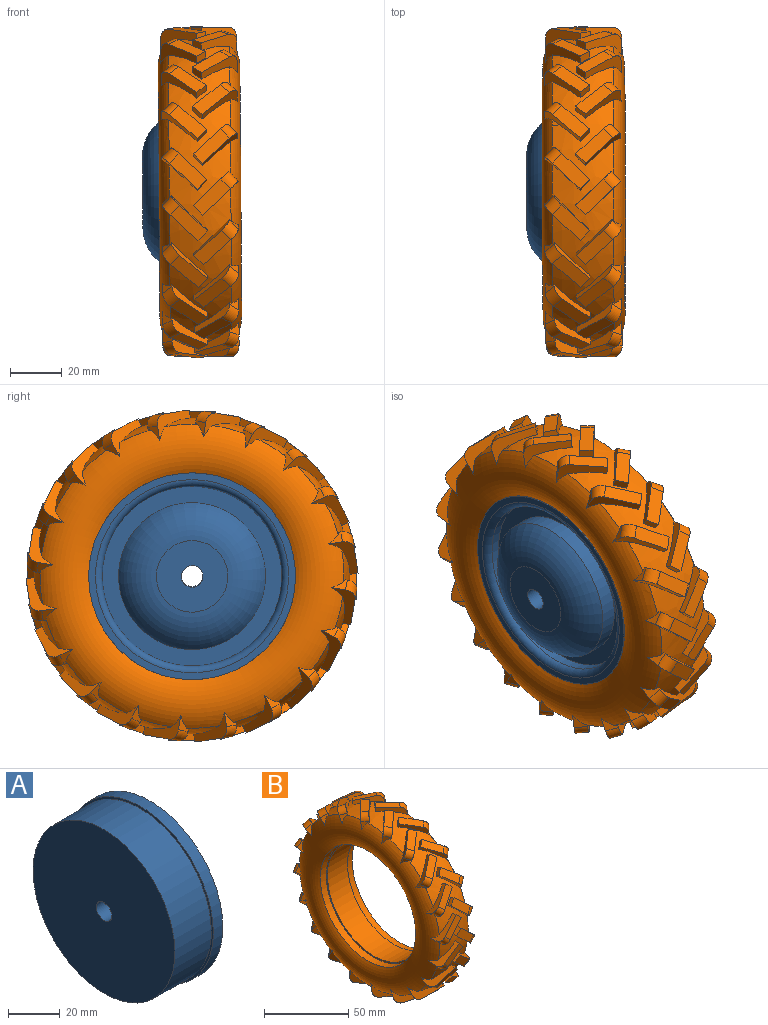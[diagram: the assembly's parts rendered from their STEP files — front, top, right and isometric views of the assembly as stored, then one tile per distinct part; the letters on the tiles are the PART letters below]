
ASSEMBLY  parts=2 mates=2
PART A: 12 faces, bbox 33.7x80.8x80.8 mm
  f0: cylinder r=39.98mm len=79.95mm, axis (1,0,0), area 1321.2mm2, adj f1,f2
  f1: plane 79.95x79.95mm, normal (-1,0,0), area 260.8mm2, adj f0,f3
  f2: plane 79.95x79.95mm, normal (1,0,0), area 638.9mm2, adj f0,f11
  f3: cylinder r=38.92mm len=77.85mm, axis (1,0,0), area 4888.4mm2, adj f1,f4
  f4: plane 77.85x77.85mm, normal (-1,0,0), area 4704.1mm2, adj f3,f7
  f5: plane 27.65x27.65mm, normal (1,0,0), area 545mm2, adj f6,f7
  f6: torus R=13.83mm, axis (-1,0,0), area 2421.4mm2, adj f5,f9
  f7: cylinder r=4.21mm len=33.66mm, axis (-1,0,0), area 890.1mm2, adj f4,f5
  f8: cylinder r=34.72mm len=69.43mm, axis (1,0,0), area 803.1mm2, adj f10,f11
  f9: cylinder r=28.4mm len=56.81mm, axis (1,0,0), area 1126.5mm2, adj f6,f10
  f10: plane 69.43x69.43mm, normal (1,0,0), area 1251.7mm2, adj f8,f9
  f11: torus R=37.35mm, axis (1,0,0), area 925.9mm2, adj f2,f8
PART B: 250 faces, bbox 31.7x129.1x129.1 mm
  f0: torus R=48.39mm, axis (-1,0,0), area 6003.5mm2, adj f2,f4,f7,f8,f19,f20,f31,f32
  f1: cylinder r=38.92mm len=77.85mm, axis (1,0,0), area 4116.5mm2, adj f247,f249
  f2: torus R=28.4mm, axis (-1,0,0), area 5449.9mm2, adj f0,f3,f4,f5,f6,f7,f8,f9
  f3: torus R=28.4mm, axis (-1,0,0), area 4.2mm2, adj f2,f5,f195
  f4: torus R=28.4mm, axis (-1,0,0), area 0.3mm2, adj f0,f2,f175
  f5: torus R=48.39mm, axis (-1,0,0), area 6003.6mm2, adj f2,f3,f14,f15,f26,f27,f38,f39
  f6: plane 13.76x12.72mm, normal (0.69,0.11,-0.72), area 58.8mm2, adj f2,f7,f9,f10,f11
  f7: plane 5.51x4.65mm, normal (-0.73,0.11,-0.68), area 13.8mm2, adj f0,f2,f6,f8,f11
  f8: plane 13.86x12.87mm, normal (-0.69,-0.11,0.72), area 77.6mm2, adj f0,f2,f7,f9,f10,f11
  f9: plane 4.29x3.63mm, normal (0.73,-0.11,0.68), area 15.9mm2, adj f2,f6,f8,f10
  f10: plane 14.32x13.77mm, normal (0,-0.99,-0.16), area 77.5mm2, adj f6,f8,f9,f11
  f11: cylinder r=4.21mm len=6.67mm, axis (0.69,0.11,-0.72), area 34.8mm2, adj f6,f7,f8,f10
  f12: plane 3.83x3.63mm, normal (-0.73,0,0.69), area 15.9mm2, adj f2,f13,f15,f16
  f13: plane 13.76x13.01mm, normal (-0.69,0,-0.73), area 58.8mm2, adj f2,f12,f14,f16,f17
  f14: plane 5.58x3.82mm, normal (0.73,0,-0.69), area 13.8mm2, adj f2,f5,f13,f15,f17
  f15: plane 13.85x13.11mm, normal (0.69,0,0.73), area 77.6mm2, adj f2,f5,f12,f14,f16,f17
  f16: plane 14.32x13.94mm, normal (0,-1,0), area 77.5mm2, adj f12,f13,f15,f17
  f17: cylinder r=4.21mm len=6.71mm, axis (-0.69,0,-0.73), area 34.8mm2, adj f13,f14,f15,f16
  f18: plane 13.76x11.63mm, normal (0.69,0.33,-0.65), area 58.8mm2, adj f2,f19,f21,f22,f23
  f19: plane 5.94x4.97mm, normal (-0.73,0.31,-0.61), area 13.8mm2, adj f0,f2,f18,f20,f23
  f20: plane 14.72x13.86mm, normal (-0.69,-0.33,0.65), area 77.6mm2, adj f0,f2,f19,f21,f22,f23
  f21: plane 4.88x4.34mm, normal (0.73,-0.31,0.61), area 15.9mm2, adj f2,f18,f20,f22
  f22: plane 14.32x12.42mm, normal (0,-0.89,-0.45), area 77.5mm2, adj f18,f20,f21,f23
  f23: cylinder r=4.21mm len=6.8mm, axis (0.69,0.33,-0.65), area 34.8mm2, adj f18,f19,f20,f22
  f24: plane 4.64x3.96mm, normal (-0.73,-0.21,0.65), area 15.9mm2, adj f2,f25,f27,f28
  f25: plane 13.76x12.26mm, normal (-0.69,0.22,-0.69), area 58.8mm2, adj f2,f24,f26,f28,f29
  f26: plane 5.36x5.3mm, normal (0.73,0.21,-0.65), area 13.8mm2, adj f2,f5,f25,f27,f29
  f27: plane 13.85x13.42mm, normal (0.69,-0.22,0.69), area 77.6mm2, adj f2,f5,f24,f26,f28,f29
  f28: plane 14.32x13.26mm, normal (0,-0.95,-0.31), area 77.5mm2, adj f24,f25,f27,f29
  f29: cylinder r=4.21mm len=6.67mm, axis (-0.69,0.22,-0.69), area 34.8mm2, adj f25,f26,f27,f28
  f30: plane 13.76x12.87mm, normal (0.69,0.51,-0.51), area 58.8mm2, adj f2,f31,f33,f34,f35
  f31: plane 6.65x3.95mm, normal (-0.73,0.49,-0.49), area 13.8mm2, adj f0,f2,f30,f32,f35
  f32: plane 16.22x13.86mm, normal (-0.69,-0.51,0.51), area 77.6mm2, adj f0,f2,f31,f33,f34,f35
  f33: plane 5x4.77mm, normal (0.73,-0.49,0.49), area 15.9mm2, adj f2,f30,f32,f34
  f34: plane 14.32x9.86mm, normal (0,-0.71,-0.71), area 77.5mm2, adj f30,f32,f33,f35
  f35: cylinder r=4.21mm len=7.72mm, axis (0.69,0.51,-0.51), area 34.8mm2, adj f30,f31,f32,f34
  f36: plane 5x4.61mm, normal (-0.73,-0.4,0.56), area 15.9mm2, adj f2,f37,f39,f40
  f37: plane 13.76x11.84mm, normal (-0.69,0.43,-0.59), area 58.8mm2, adj f2,f36,f38,f40,f41
  f38: plane 6.37x4.51mm, normal (0.73,0.4,-0.56), area 13.8mm2, adj f2,f5,f37,f39,f41
  f39: plane 15.66x13.85mm, normal (0.69,-0.43,0.59), area 77.6mm2, adj f2,f5,f36,f38,f40,f41
  f40: plane 14.32x11.28mm, normal (0,-0.81,-0.59), area 77.5mm2, adj f36,f37,f39,f41
  f41: cylinder r=4.21mm len=7.35mm, axis (-0.69,0.43,-0.59), area 34.8mm2, adj f37,f38,f39,f40
  f42: plane 13.95x13.76mm, normal (0.69,0.65,-0.33), area 58.8mm2, adj f2,f43,f45,f46,f47
  f43: plane 6.71x3.85mm, normal (-0.73,0.61,-0.31), area 13.8mm2, adj f0,f2,f42,f44,f47
  f44: plane 16.14x13.86mm, normal (-0.69,-0.65,0.33), area 77.6mm2, adj f0,f2,f43,f45,f46,f47
  f45: plane 4.74x4.62mm, normal (0.73,-0.61,0.31), area 15.9mm2, adj f2,f42,f44,f46
  f46: plane 14.32x12.42mm, normal (0,-0.45,-0.89), area 77.5mm2, adj f42,f44,f45,f47
  f47: cylinder r=4.21mm len=7.89mm, axis (0.69,0.65,-0.33), area 34.8mm2, adj f42,f43,f44,f46
  f48: plane 4.87x4.81mm, normal (-0.73,-0.56,0.4), area 15.9mm2, adj f2,f49,f51,f52
  f49: plane 13.76x13.57mm, normal (-0.69,0.59,-0.43), area 58.8mm2, adj f2,f48,f50,f52,f53
  f50: plane 6.76x3.67mm, normal (0.73,0.56,-0.4), area 13.8mm2, adj f2,f5,f49,f51,f53
  f51: plane 16.37x13.85mm, normal (0.69,-0.59,0.43), area 77.6mm2, adj f2,f5,f48,f50,f52,f53
  f52: plane 14.32x11.28mm, normal (0,-0.59,-0.81), area 77.5mm2, adj f48,f49,f51,f53
  f53: cylinder r=4.21mm len=7.9mm, axis (-0.69,0.59,-0.43), area 34.8mm2, adj f49,f50,f51,f52
  f54: plane 13.76x13.66mm, normal (0.69,0.72,-0.11), area 58.8mm2, adj f2,f55,f57,f58,f59
  f55: plane 6.11x3.93mm, normal (-0.73,0.68,-0.11), area 13.8mm2, adj f0,f2,f54,f56,f59
  f56: plane 14.48x13.86mm, normal (-0.69,-0.72,0.11), area 77.6mm2, adj f0,f2,f55,f57,f58,f59
  f57: plane 4.24x3.8mm, normal (0.73,-0.68,0.11), area 15.9mm2, adj f2,f54,f56,f58
  f58: plane 14.32x13.77mm, normal (0,-0.16,-0.99), area 77.5mm2, adj f54,f56,f57,f59
  f59: cylinder r=4.21mm len=7.29mm, axis (0.69,0.72,-0.11), area 34.8mm2, adj f54,f55,f56,f58
  f60: plane 4.55x4.26mm, normal (-0.73,-0.65,0.21), area 15.9mm2, adj f2,f61,f63,f64
  f61: plane 13.98x13.76mm, normal (-0.69,0.69,-0.22), area 58.8mm2, adj f2,f60,f62,f64,f65
  f62: plane 6.49x3.94mm, normal (0.73,0.65,-0.21), area 13.8mm2, adj f2,f5,f61,f63,f65
  f63: plane 15.49x13.85mm, normal (0.69,-0.69,0.22), area 77.6mm2, adj f2,f5,f60,f62,f64,f65
  f64: plane 14.32x13.26mm, normal (0,-0.31,-0.95), area 77.5mm2, adj f60,f61,f63,f65
  f65: cylinder r=4.21mm len=7.69mm, axis (-0.69,0.69,-0.22), area 34.8mm2, adj f61,f62,f63,f64
  f66: plane 13.76x12.72mm, normal (0.69,0.72,0.11), area 58.8mm2, adj f2,f67,f69,f70,f71
  f67: plane 5.51x4.65mm, normal (-0.73,0.68,0.11), area 13.8mm2, adj f0,f2,f66,f68,f71
  f68: plane 13.86x12.87mm, normal (-0.69,-0.72,-0.11), area 77.6mm2, adj f0,f2,f67,f69,f70,f71
  f69: plane 4.29x3.63mm, normal (0.73,-0.68,-0.11), area 15.9mm2, adj f2,f66,f68,f70
  f70: plane 14.32x13.77mm, normal (0,0.16,-0.99), area 77.5mm2, adj f66,f68,f69,f71
  f71: cylinder r=4.21mm len=6.67mm, axis (0.69,0.72,0.11), area 34.8mm2, adj f66,f67,f68,f70
  f72: plane 3.83x3.63mm, normal (-0.73,-0.69,0), area 15.9mm2, adj f2,f73,f75,f76
  f73: plane 13.76x13.01mm, normal (-0.69,0.73,0), area 58.8mm2, adj f2,f72,f74,f76,f77
  f74: plane 5.58x3.82mm, normal (0.73,0.69,0), area 13.8mm2, adj f2,f5,f73,f75,f77
  f75: plane 13.85x13.11mm, normal (0.69,-0.73,0), area 77.6mm2, adj f2,f5,f72,f74,f76,f77
  f76: plane 14.32x13.94mm, normal (0,0,-1), area 77.5mm2, adj f72,f73,f75,f77
  f77: cylinder r=4.21mm len=6.71mm, axis (-0.69,0.73,0), area 34.8mm2, adj f73,f74,f75,f76
  f78: plane 13.76x11.63mm, normal (0.69,0.65,0.33), area 58.8mm2, adj f2,f79,f81,f82,f83
  f79: plane 5.94x4.97mm, normal (-0.73,0.61,0.31), area 13.8mm2, adj f0,f2,f78,f80,f83
  f80: plane 14.72x13.86mm, normal (-0.69,-0.65,-0.33), area 77.6mm2, adj f0,f2,f79,f81,f82,f83
  f81: plane 4.88x4.34mm, normal (0.73,-0.61,-0.31), area 15.9mm2, adj f2,f78,f80,f82
  f82: plane 14.32x12.42mm, normal (0,0.45,-0.89), area 77.5mm2, adj f78,f80,f81,f83
  f83: cylinder r=4.21mm len=6.8mm, axis (0.69,0.65,0.33), area 34.8mm2, adj f78,f79,f80,f82
  f84: plane 4.64x3.96mm, normal (-0.73,-0.65,-0.21), area 15.9mm2, adj f2,f85,f87,f88
  f85: plane 13.76x12.26mm, normal (-0.69,0.69,0.22), area 58.8mm2, adj f2,f84,f86,f88,f89
  f86: plane 5.36x5.3mm, normal (0.73,0.65,0.21), area 13.8mm2, adj f2,f5,f85,f87,f89
  f87: plane 13.85x13.42mm, normal (0.69,-0.69,-0.22), area 77.6mm2, adj f2,f5,f84,f86,f88,f89
  f88: plane 14.32x13.26mm, normal (0,0.31,-0.95), area 77.5mm2, adj f84,f85,f87,f89
  f89: cylinder r=4.21mm len=6.67mm, axis (-0.69,0.69,0.22), area 34.8mm2, adj f85,f86,f87,f88
  f90: plane 13.76x12.87mm, normal (0.69,0.51,0.51), area 58.8mm2, adj f2,f91,f93,f94,f95
  f91: plane 6.65x3.95mm, normal (-0.73,0.49,0.49), area 13.8mm2, adj f0,f2,f90,f92,f95
  f92: plane 16.22x13.86mm, normal (-0.69,-0.51,-0.51), area 77.6mm2, adj f0,f2,f91,f93,f94,f95
  f93: plane 5x4.77mm, normal (0.73,-0.49,-0.49), area 15.9mm2, adj f2,f90,f92,f94
  f94: plane 14.32x9.86mm, normal (0,0.71,-0.71), area 77.5mm2, adj f90,f92,f93,f95
  f95: cylinder r=4.21mm len=7.72mm, axis (0.69,0.51,0.51), area 34.8mm2, adj f90,f91,f92,f94
  f96: plane 5x4.61mm, normal (-0.73,-0.56,-0.4), area 15.9mm2, adj f2,f97,f99,f100
  f97: plane 13.76x11.84mm, normal (-0.69,0.59,0.43), area 58.8mm2, adj f2,f96,f98,f100,f101
  f98: plane 6.37x4.51mm, normal (0.73,0.56,0.4), area 13.8mm2, adj f2,f5,f97,f99,f101
  f99: plane 15.66x13.85mm, normal (0.69,-0.59,-0.43), area 77.6mm2, adj f2,f5,f96,f98,f100,f101
  f100: plane 14.32x11.28mm, normal (0,0.59,-0.81), area 77.5mm2, adj f96,f97,f99,f101
  f101: cylinder r=4.21mm len=7.35mm, axis (-0.69,0.59,0.43), area 34.8mm2, adj f97,f98,f99,f100
  f102: plane 13.95x13.76mm, normal (0.69,0.33,0.65), area 58.8mm2, adj f2,f103,f105,f106,f107
  f103: plane 6.71x3.85mm, normal (-0.73,0.31,0.61), area 13.8mm2, adj f0,f2,f102,f104,f107
  f104: plane 16.14x13.86mm, normal (-0.69,-0.33,-0.65), area 77.6mm2, adj f0,f2,f103,f105,f106,f107
  f105: plane 4.74x4.62mm, normal (0.73,-0.31,-0.61), area 15.9mm2, adj f2,f102,f104,f106
  f106: plane 14.32x12.42mm, normal (0,0.89,-0.45), area 77.5mm2, adj f102,f104,f105,f107
  f107: cylinder r=4.21mm len=7.89mm, axis (0.69,0.33,0.65), area 34.8mm2, adj f102,f103,f104,f106
  f108: plane 4.87x4.81mm, normal (-0.73,-0.4,-0.56), area 15.9mm2, adj f2,f109,f111,f112
  f109: plane 13.76x13.57mm, normal (-0.69,0.43,0.59), area 58.8mm2, adj f2,f108,f110,f112,f113
  f110: plane 6.76x3.67mm, normal (0.73,0.4,0.56), area 13.8mm2, adj f2,f5,f109,f111,f113
  f111: plane 16.37x13.85mm, normal (0.69,-0.43,-0.59), area 77.6mm2, adj f2,f5,f108,f110,f112,f113
  f112: plane 14.32x11.28mm, normal (0,0.81,-0.59), area 77.5mm2, adj f108,f109,f111,f113
  f113: cylinder r=4.21mm len=7.9mm, axis (-0.69,0.43,0.59), area 34.8mm2, adj f109,f110,f111,f112
  f114: plane 13.76x13.66mm, normal (0.69,0.11,0.72), area 58.8mm2, adj f2,f115,f117,f118,f119
  f115: plane 6.11x3.93mm, normal (-0.73,0.11,0.68), area 13.8mm2, adj f0,f2,f114,f116,f119
  f116: plane 14.48x13.86mm, normal (-0.69,-0.11,-0.72), area 77.6mm2, adj f0,f2,f115,f117,f118,f119
  f117: plane 4.24x3.8mm, normal (0.73,-0.11,-0.68), area 15.9mm2, adj f2,f114,f116,f118
  f118: plane 14.32x13.77mm, normal (0,0.99,-0.16), area 77.5mm2, adj f114,f116,f117,f119
  f119: cylinder r=4.21mm len=7.29mm, axis (0.69,0.11,0.72), area 34.8mm2, adj f114,f115,f116,f118
  f120: plane 4.55x4.26mm, normal (-0.73,-0.21,-0.65), area 15.9mm2, adj f2,f121,f123,f124
  f121: plane 13.98x13.76mm, normal (-0.69,0.22,0.69), area 58.8mm2, adj f2,f120,f122,f124,f125
  f122: plane 6.49x3.94mm, normal (0.73,0.21,0.65), area 13.8mm2, adj f2,f5,f121,f123,f125
  f123: plane 15.49x13.85mm, normal (0.69,-0.22,-0.69), area 77.6mm2, adj f2,f5,f120,f122,f124,f125
  f124: plane 14.32x13.26mm, normal (0,0.95,-0.31), area 77.5mm2, adj f120,f121,f123,f125
  f125: cylinder r=4.21mm len=7.69mm, axis (-0.69,0.22,0.69), area 34.8mm2, adj f121,f122,f123,f124
  f126: plane 13.76x12.72mm, normal (0.69,-0.11,0.72), area 58.8mm2, adj f2,f127,f129,f130,f131
  f127: plane 5.51x4.65mm, normal (-0.73,-0.11,0.68), area 13.8mm2, adj f0,f2,f126,f128,f131
  f128: plane 13.86x12.87mm, normal (-0.69,0.11,-0.72), area 77.6mm2, adj f0,f2,f127,f129,f130,f131
  f129: plane 4.29x3.63mm, normal (0.73,0.11,-0.68), area 15.9mm2, adj f2,f126,f128,f130
  f130: plane 14.32x13.77mm, normal (0,0.99,0.16), area 77.5mm2, adj f126,f128,f129,f131
  f131: cylinder r=4.21mm len=6.67mm, axis (0.69,-0.11,0.72), area 34.8mm2, adj f126,f127,f128,f130
  f132: plane 3.83x3.63mm, normal (-0.73,0,-0.69), area 15.9mm2, adj f2,f133,f135,f136
  f133: plane 13.76x13.01mm, normal (-0.69,0,0.73), area 58.8mm2, adj f2,f132,f134,f136,f137
  f134: plane 5.58x3.82mm, normal (0.73,0,0.69), area 13.8mm2, adj f2,f5,f133,f135,f137
  f135: plane 13.85x13.11mm, normal (0.69,0,-0.73), area 77.6mm2, adj f2,f5,f132,f134,f136,f137
  f136: plane 14.32x13.94mm, normal (0,1,0), area 77.5mm2, adj f132,f133,f135,f137
  f137: cylinder r=4.21mm len=6.71mm, axis (-0.69,0,0.73), area 34.8mm2, adj f133,f134,f135,f136
  f138: plane 13.76x11.63mm, normal (0.69,-0.33,0.65), area 58.8mm2, adj f2,f139,f141,f142,f143
  f139: plane 5.94x4.97mm, normal (-0.73,-0.31,0.61), area 13.8mm2, adj f0,f2,f138,f140,f143
  f140: plane 14.72x13.86mm, normal (-0.69,0.33,-0.65), area 77.6mm2, adj f0,f2,f139,f141,f142,f143
  f141: plane 4.88x4.34mm, normal (0.73,0.31,-0.61), area 15.9mm2, adj f2,f138,f140,f142
  f142: plane 14.32x12.42mm, normal (0,0.89,0.45), area 77.5mm2, adj f138,f140,f141,f143
  f143: cylinder r=4.21mm len=6.8mm, axis (0.69,-0.33,0.65), area 34.8mm2, adj f138,f139,f140,f142
  f144: plane 4.64x3.96mm, normal (-0.73,0.21,-0.65), area 15.9mm2, adj f2,f145,f147,f148
  f145: plane 13.76x12.26mm, normal (-0.69,-0.22,0.69), area 58.8mm2, adj f2,f144,f146,f148,f149
  f146: plane 5.36x5.3mm, normal (0.73,-0.21,0.65), area 13.8mm2, adj f2,f5,f145,f147,f149
  f147: plane 13.85x13.42mm, normal (0.69,0.22,-0.69), area 77.6mm2, adj f2,f5,f144,f146,f148,f149
  f148: plane 14.32x13.26mm, normal (0,0.95,0.31), area 77.5mm2, adj f144,f145,f147,f149
  f149: cylinder r=4.21mm len=6.67mm, axis (-0.69,-0.22,0.69), area 34.8mm2, adj f145,f146,f147,f148
  f150: plane 13.76x12.87mm, normal (0.69,-0.51,0.51), area 58.8mm2, adj f2,f151,f153,f154,f155
  f151: plane 6.65x3.95mm, normal (-0.73,-0.49,0.49), area 13.8mm2, adj f0,f2,f150,f152,f155
  f152: plane 16.22x13.86mm, normal (-0.69,0.51,-0.51), area 77.6mm2, adj f0,f2,f151,f153,f154,f155
  f153: plane 5x4.77mm, normal (0.73,0.49,-0.49), area 15.9mm2, adj f2,f150,f152,f154
  f154: plane 14.32x9.86mm, normal (0,0.71,0.71), area 77.5mm2, adj f150,f152,f153,f155
  f155: cylinder r=4.21mm len=7.72mm, axis (0.69,-0.51,0.51), area 34.8mm2, adj f150,f151,f152,f154
  f156: plane 5x4.61mm, normal (-0.73,0.4,-0.56), area 15.9mm2, adj f2,f157,f159,f160
  f157: plane 13.76x11.84mm, normal (-0.69,-0.43,0.59), area 58.8mm2, adj f2,f156,f158,f160,f161
  f158: plane 6.37x4.51mm, normal (0.73,-0.4,0.56), area 13.8mm2, adj f2,f5,f157,f159,f161
  f159: plane 15.66x13.85mm, normal (0.69,0.43,-0.59), area 77.6mm2, adj f2,f5,f156,f158,f160,f161
  f160: plane 14.32x11.28mm, normal (0,0.81,0.59), area 77.5mm2, adj f156,f157,f159,f161
  f161: cylinder r=4.21mm len=7.35mm, axis (-0.69,-0.43,0.59), area 34.8mm2, adj f157,f158,f159,f160
  f162: plane 13.95x13.76mm, normal (0.69,-0.65,0.33), area 58.8mm2, adj f2,f163,f165,f166,f167
  f163: plane 6.71x3.85mm, normal (-0.73,-0.61,0.31), area 13.8mm2, adj f0,f2,f162,f164,f167
  f164: plane 16.14x13.86mm, normal (-0.69,0.65,-0.33), area 77.6mm2, adj f0,f2,f163,f165,f166,f167
  f165: plane 4.74x4.62mm, normal (0.73,0.61,-0.31), area 15.9mm2, adj f2,f162,f164,f166
  f166: plane 14.32x12.42mm, normal (0,0.45,0.89), area 77.5mm2, adj f162,f164,f165,f167
  f167: cylinder r=4.21mm len=7.89mm, axis (0.69,-0.65,0.33), area 34.8mm2, adj f162,f163,f164,f166
  f168: plane 4.87x4.81mm, normal (-0.73,0.56,-0.4), area 15.9mm2, adj f2,f169,f171,f172
  f169: plane 13.76x13.57mm, normal (-0.69,-0.59,0.43), area 58.8mm2, adj f2,f168,f170,f172,f173
  f170: plane 6.76x3.67mm, normal (0.73,-0.56,0.4), area 13.8mm2, adj f2,f5,f169,f171,f173
  f171: plane 16.37x13.85mm, normal (0.69,0.59,-0.43), area 77.6mm2, adj f2,f5,f168,f170,f172,f173
  f172: plane 14.32x11.28mm, normal (0,0.59,0.81), area 77.5mm2, adj f168,f169,f171,f173
  f173: cylinder r=4.21mm len=7.9mm, axis (-0.69,-0.59,0.43), area 34.8mm2, adj f169,f170,f171,f172
  f174: plane 13.76x13.66mm, normal (0.69,-0.72,0.11), area 58.8mm2, adj f2,f175,f177,f178,f179
  f175: plane 6.11x3.93mm, normal (-0.73,-0.68,0.11), area 13.8mm2, adj f0,f4,f174,f176,f179
  f176: plane 14.48x13.86mm, normal (-0.69,0.72,-0.11), area 77.6mm2, adj f0,f2,f175,f177,f178,f179
  f177: plane 4.24x3.8mm, normal (0.73,0.68,-0.11), area 15.9mm2, adj f2,f174,f176,f178
  f178: plane 14.32x13.77mm, normal (0,0.16,0.99), area 77.5mm2, adj f174,f176,f177,f179
  f179: cylinder r=4.21mm len=7.29mm, axis (0.69,-0.72,0.11), area 34.8mm2, adj f174,f175,f176,f178
  f180: plane 4.55x4.26mm, normal (-0.73,0.65,-0.21), area 15.9mm2, adj f2,f181,f183,f184
  f181: plane 13.98x13.76mm, normal (-0.69,-0.69,0.22), area 58.8mm2, adj f2,f180,f182,f184,f185
  f182: plane 6.49x3.94mm, normal (0.73,-0.65,0.21), area 13.8mm2, adj f2,f5,f181,f183,f185
  f183: plane 15.49x13.85mm, normal (0.69,0.69,-0.22), area 77.6mm2, adj f2,f5,f180,f182,f184,f185
  f184: plane 14.32x13.26mm, normal (0,0.31,0.95), area 77.5mm2, adj f180,f181,f183,f185
  f185: cylinder r=4.21mm len=7.69mm, axis (-0.69,-0.69,0.22), area 34.8mm2, adj f181,f182,f183,f184
  f186: plane 13.76x12.72mm, normal (0.69,-0.72,-0.11), area 58.8mm2, adj f2,f187,f189,f190,f191
  f187: plane 5.51x4.65mm, normal (-0.73,-0.68,-0.11), area 13.8mm2, adj f0,f2,f186,f188,f191
  f188: plane 13.86x12.87mm, normal (-0.69,0.72,0.11), area 77.6mm2, adj f0,f2,f187,f189,f190,f191
  f189: plane 4.29x3.63mm, normal (0.73,0.68,0.11), area 15.9mm2, adj f2,f186,f188,f190
  f190: plane 14.32x13.77mm, normal (0,-0.16,0.99), area 77.5mm2, adj f186,f188,f189,f191
  f191: cylinder r=4.21mm len=6.67mm, axis (0.69,-0.72,-0.11), area 34.8mm2, adj f186,f187,f188,f190
  f192: plane 3.83x3.63mm, normal (-0.73,0.69,0), area 15.9mm2, adj f2,f193,f195,f196
  f193: plane 13.78x13.03mm, normal (-0.69,-0.73,0), area 58.8mm2, adj f2,f192,f194,f196,f197
  f194: plane 5.58x3.82mm, normal (0.73,-0.69,0), area 13.8mm2, adj f2,f5,f193,f195,f197
  f195: plane 13.8x13.05mm, normal (0.69,0.73,0), area 77.6mm2, adj f2,f3,f5,f192,f194,f196,f197
  f196: plane 14.32x13.94mm, normal (0,0,1), area 77.5mm2, adj f192,f193,f195,f197
  f197: cylinder r=4.21mm len=6.71mm, axis (-0.69,-0.73,0), area 34.8mm2, adj f193,f194,f195,f196
  f198: plane 13.76x11.63mm, normal (0.69,-0.65,-0.33), area 58.8mm2, adj f2,f199,f201,f202,f203
  f199: plane 5.94x4.97mm, normal (-0.73,-0.61,-0.31), area 13.8mm2, adj f0,f2,f198,f200,f203
  f200: plane 14.72x13.86mm, normal (-0.69,0.65,0.33), area 77.6mm2, adj f0,f2,f199,f201,f202,f203
  f201: plane 4.88x4.34mm, normal (0.73,0.61,0.31), area 15.9mm2, adj f2,f198,f200,f202
  f202: plane 14.32x12.42mm, normal (0,-0.45,0.89), area 77.5mm2, adj f198,f200,f201,f203
  f203: cylinder r=4.21mm len=6.8mm, axis (0.69,-0.65,-0.33), area 34.8mm2, adj f198,f199,f200,f202
  f204: plane 4.64x3.96mm, normal (-0.73,0.65,0.21), area 15.9mm2, adj f2,f205,f207,f208
  f205: plane 13.76x12.26mm, normal (-0.69,-0.69,-0.22), area 58.8mm2, adj f2,f204,f206,f208,f209
  f206: plane 5.36x5.3mm, normal (0.73,-0.65,-0.21), area 13.8mm2, adj f2,f5,f205,f207,f209
  f207: plane 13.85x13.42mm, normal (0.69,0.69,0.22), area 77.6mm2, adj f2,f5,f204,f206,f208,f209
  f208: plane 14.32x13.26mm, normal (0,-0.31,0.95), area 77.5mm2, adj f204,f205,f207,f209
  f209: cylinder r=4.21mm len=6.67mm, axis (-0.69,-0.69,-0.22), area 34.8mm2, adj f205,f206,f207,f208
  f210: plane 13.76x12.87mm, normal (0.69,-0.51,-0.51), area 58.8mm2, adj f2,f211,f213,f214,f215
  f211: plane 6.65x3.95mm, normal (-0.73,-0.49,-0.49), area 13.8mm2, adj f0,f2,f210,f212,f215
  f212: plane 16.22x13.86mm, normal (-0.69,0.51,0.51), area 77.6mm2, adj f0,f2,f211,f213,f214,f215
  f213: plane 5x4.77mm, normal (0.73,0.49,0.49), area 15.9mm2, adj f2,f210,f212,f214
  f214: plane 14.32x9.86mm, normal (0,-0.71,0.71), area 77.5mm2, adj f210,f212,f213,f215
  f215: cylinder r=4.21mm len=7.72mm, axis (0.69,-0.51,-0.51), area 34.8mm2, adj f210,f211,f212,f214
  f216: plane 5x4.61mm, normal (-0.73,0.56,0.4), area 15.9mm2, adj f2,f217,f219,f220
  f217: plane 13.76x11.84mm, normal (-0.69,-0.59,-0.43), area 58.8mm2, adj f2,f216,f218,f220,f221
  f218: plane 6.37x4.51mm, normal (0.73,-0.56,-0.4), area 13.8mm2, adj f2,f5,f217,f219,f221
  f219: plane 15.66x13.85mm, normal (0.69,0.59,0.43), area 77.6mm2, adj f2,f5,f216,f218,f220,f221
  f220: plane 14.32x11.28mm, normal (0,-0.59,0.81), area 77.5mm2, adj f216,f217,f219,f221
  f221: cylinder r=4.21mm len=7.35mm, axis (-0.69,-0.59,-0.43), area 34.8mm2, adj f217,f218,f219,f220
  f222: plane 13.95x13.76mm, normal (0.69,-0.33,-0.65), area 58.8mm2, adj f2,f223,f225,f226,f227
  f223: plane 6.71x3.85mm, normal (-0.73,-0.31,-0.61), area 13.8mm2, adj f0,f2,f222,f224,f227
  f224: plane 16.14x13.86mm, normal (-0.69,0.33,0.65), area 77.6mm2, adj f0,f2,f223,f225,f226,f227
  f225: plane 4.74x4.62mm, normal (0.73,0.31,0.61), area 15.9mm2, adj f2,f222,f224,f226
  f226: plane 14.32x12.42mm, normal (0,-0.89,0.45), area 77.5mm2, adj f222,f224,f225,f227
  f227: cylinder r=4.21mm len=7.89mm, axis (0.69,-0.33,-0.65), area 34.8mm2, adj f222,f223,f224,f226
  f228: plane 4.87x4.81mm, normal (-0.73,0.4,0.56), area 15.9mm2, adj f2,f229,f231,f232
  f229: plane 13.76x13.57mm, normal (-0.69,-0.43,-0.59), area 58.8mm2, adj f2,f228,f230,f232,f233
  f230: plane 6.76x3.67mm, normal (0.73,-0.4,-0.56), area 13.8mm2, adj f2,f5,f229,f231,f233
  f231: plane 16.37x13.85mm, normal (0.69,0.43,0.59), area 77.6mm2, adj f2,f5,f228,f230,f232,f233
  f232: plane 14.32x11.28mm, normal (0,-0.81,0.59), area 77.5mm2, adj f228,f229,f231,f233
  f233: cylinder r=4.21mm len=7.9mm, axis (-0.69,-0.43,-0.59), area 34.8mm2, adj f229,f230,f231,f232
  f234: plane 13.76x13.66mm, normal (0.69,-0.11,-0.72), area 58.8mm2, adj f2,f235,f237,f238,f239
  f235: plane 6.11x3.93mm, normal (-0.73,-0.11,-0.68), area 13.8mm2, adj f0,f2,f234,f236,f239
  f236: plane 14.48x13.86mm, normal (-0.69,0.11,0.72), area 77.6mm2, adj f0,f2,f235,f237,f238,f239
  f237: plane 4.24x3.8mm, normal (0.73,0.11,0.68), area 15.9mm2, adj f2,f234,f236,f238
  f238: plane 14.32x13.77mm, normal (0,-0.99,0.16), area 77.5mm2, adj f234,f236,f237,f239
  f239: cylinder r=4.21mm len=7.29mm, axis (0.69,-0.11,-0.72), area 34.8mm2, adj f234,f235,f236,f238
  f240: plane 4.55x4.26mm, normal (-0.73,0.21,0.65), area 15.9mm2, adj f2,f241,f243,f244
  f241: plane 13.98x13.76mm, normal (-0.69,-0.22,-0.69), area 58.8mm2, adj f2,f240,f242,f244,f245
  f242: plane 6.49x3.94mm, normal (0.73,-0.21,-0.65), area 13.8mm2, adj f2,f5,f241,f243,f245
  f243: plane 15.49x13.85mm, normal (0.69,0.22,0.69), area 77.6mm2, adj f2,f5,f240,f242,f244,f245
  f244: plane 14.32x13.26mm, normal (0,-0.95,0.31), area 77.5mm2, adj f240,f241,f243,f245
  f245: cylinder r=4.21mm len=7.69mm, axis (-0.69,-0.22,-0.69), area 34.8mm2, adj f241,f242,f243,f244
  f246: cylinder r=39.98mm len=79.95mm, axis (1,0,0), area 1238.9mm2, adj f5,f247
  f247: plane 79.95x79.95mm, normal (1,0,0), area 260.8mm2, adj f1,f246
  f248: cylinder r=39.98mm len=79.95mm, axis (-1,0,0), area 1238.9mm2, adj f0,f249
  f249: plane 79.95x79.95mm, normal (-1,0,0), area 260.8mm2, adj f1,f248
PLACE A rot(axis=(0,0.85,0.53),179.7deg) t=(-1730.47,-2553.88,3134)mm
PLACE B rot(axis=(0,-0.23,-0.97),180deg) t=(-1716.79,-2553.85,3134.09)mm
MATE planar A.f0 <-> B.f246  axis (1,0,0.01) through (-1725.21,-2553.87,3134.03)mm
MATE cylindrical A.f3 <-> B.f0  axis (-1,0,-0.01) through (-1715.21,-2553.85,3134.1)mm
